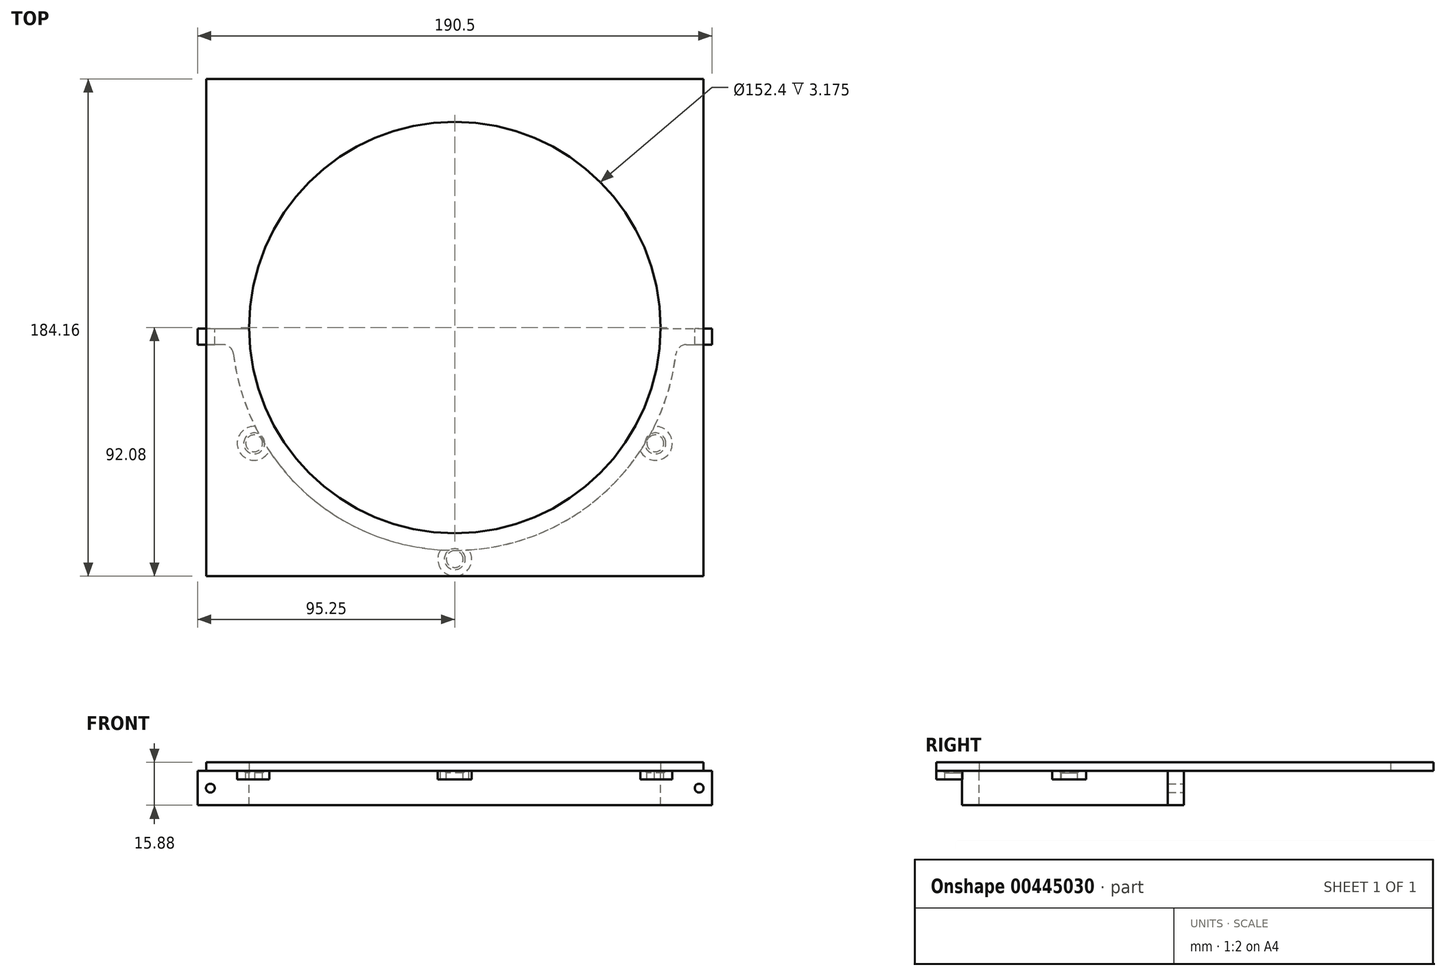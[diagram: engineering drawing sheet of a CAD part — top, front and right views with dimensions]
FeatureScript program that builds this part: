
annotation { "Feature Type Name" : "Feature", "Feature Type Description" : "" }
export const myFeature = defineFeature(function(context is Context, id is Id, definition is map)
    precondition{}
    {
        {
            var Q0;
            Q0=qCreatedBy(makeId("Top.planeOp"),FACE);
            var sketch = newSketch(context, id + "F0", { "sketchPlane" : qUnion([Q0])});
            skCircle(sketch, "E0", {"center": v(0, 0) * mm, "radius": 76.2 * mm});
            skCircle(sketch, "E1", {"center": v(0, 0) * mm, "radius": 82.55 * mm});
            skLineSegment(sketch, "E2.bottom", {"start": v(76.2, -6.35) * mm, "end": v(95.25, -6.35) * mm});
            skLineSegment(sketch, "E2.top", {"start": v(76.2, 6.35) * mm, "end": v(95.25, 6.35) * mm});
            skLineSegment(sketch, "E2.left", {"start": v(76.2, -6.35) * mm, "end": v(76.2, 6.35) * mm});
            skLineSegment(sketch, "E2.right", {"start": v(95.25, -6.35) * mm, "end": v(95.25, 6.35) * mm});
            skPoint(sketch, "E3", {"position": v(76.2, 0) * mm});
            skLineSegment(sketch, "E4.MirrorCS", {"start": v(-95.25, -6.35) * mm, "end": v(-95.25, 6.35) * mm});
            skLineSegment(sketch, "E5.MirrorCS", {"start": v(-76.2, -6.35) * mm, "end": v(-95.25, -6.35) * mm});
            skLineSegment(sketch, "E6.MirrorCS", {"start": v(-76.2, 6.35) * mm, "end": v(-95.25, 6.35) * mm});
            skCircle(sketch, "E7", {"center": v(-74.3, 42.9) * mm, "radius": 3.11 * mm});
            skLineSegment(sketch, "E8", {"start": v(-74.3, 42.9) * mm, "end": v(0, 0) * mm, "construction": true});
            skLineSegment(sketch, "E9", {"start": v(0, 0) * mm, "end": v(76.2, 0) * mm, "construction": true});
            skCircle(sketch, "E10.0", {"center": v(-74.3, 42.9) * mm, "radius": 6.29 * mm});
            skCircle(sketch, "E11.1.0", {"center": v(0, 85.79) * mm, "radius": 6.29 * mm});
            skCircle(sketch, "E11.1.1", {"center": v(0, 85.79) * mm, "radius": 3.11 * mm});
            skCircle(sketch, "E11.2.0", {"center": v(74.3, 42.9) * mm, "radius": 6.29 * mm});
            skCircle(sketch, "E11.2.1", {"center": v(74.3, 42.9) * mm, "radius": 3.11 * mm});
            skCircle(sketch, "E11.3.0", {"center": v(74.3, -42.9) * mm, "radius": 6.29 * mm});
            skCircle(sketch, "E11.3.1", {"center": v(74.3, -42.9) * mm, "radius": 3.11 * mm});
            skLineSegment(sketch, "E11.anchor2", {"start": v(-74.3, -42.9) * mm, "end": v(0, 0) * mm, "construction": true});
            skCircle(sketch, "E12.1.4.0", {"center": v(0, -85.79) * mm, "radius": 6.29 * mm});
            skCircle(sketch, "E12.2.4.0", {"center": v(0, -85.79) * mm, "radius": 3.11 * mm});
            skCircle(sketch, "E12.1.5.0", {"center": v(-74.3, -42.9) * mm, "radius": 6.29 * mm});
            skCircle(sketch, "E12.2.5.0", {"center": v(-74.3, -42.9) * mm, "radius": 3.11 * mm});
            skSolve(sketch);
        }
        {
            var Q0;
            Q0=makeQuery(id+"F0.imprint","IMPRINT",FACE,{"disambiguationData":[TD([[makeQuery(id+"F0.imprint","IMPRINT",EDGE,{"derivedFrom":sQuery(id+"F0.wireOp",EDGE,"E0")}),-1.0]])]});
            var Q1;
            {var subQ5=sQuery(id+"F0.wireOp",EDGE,"E2.right");Q1=makeQuery(id+"F0.imprint","IMPRINT",FACE,{"disambiguationData":[TD([[makeQuery(id+"F0.imprint","IMPRINT",EDGE,{"derivedFrom":subQ5}),1.0]])]});}
            var Q2;
            {var subQ3=sQuery(id+"F0.wireOp",EDGE,"E1");var subQ5=sQuery(id+"F0.wireOp",EDGE,"E2.bottom");var subQ7=makeQuery(id+"F0.imprint","INTERSECT",VERTEX,{"derivedFrom":[subQ3,subQ5]});Q2=makeQuery(id+"F0.imprint","IMPRINT",FACE,{"disambiguationData":[TD([[makeQuery(id+"F0.imprint","IMPRINT",EDGE,{"disambiguationData":[TD([[subQ7,-1.0]])],"derivedFrom":subQ3}),1.0]])]});}
            var Q3;
            {var subQ5=sQuery(id+"F0.wireOp",EDGE,"E4.MirrorCS");Q3=makeQuery(id+"F0.imprint","IMPRINT",FACE,{"disambiguationData":[TD([[makeQuery(id+"F0.imprint","IMPRINT",EDGE,{"derivedFrom":subQ5}),-1.0]])]});}
            var Q4;
            {var subQ0=sQuery(id+"F0.wireOp",EDGE,"E10.0");var subQ1=sQuery(id+"F0.wireOp",EDGE,"E1");var subQ2=makeQuery(id+"F0.imprint","INTERSECT",VERTEX,{"disambiguationData":[OD(0.0)],"derivedFrom":[subQ1,subQ0]});Q4=makeQuery(id+"F0.imprint","IMPRINT",FACE,{"disambiguationData":[TD([[makeQuery(id+"F0.imprint","IMPRINT",EDGE,{"disambiguationData":[TD([[subQ2,-1.0]])],"derivedFrom":subQ1}),1.0]])]});}
            var Q5;
            {var subQ0=sQuery(id+"F0.wireOp",EDGE,"E11.1.0");var subQ1=sQuery(id+"F0.wireOp",EDGE,"E1");var subQ2=makeQuery(id+"F0.imprint","INTERSECT",VERTEX,{"disambiguationData":[OD(0.0)],"derivedFrom":[subQ1,subQ0]});Q5=makeQuery(id+"F0.imprint","IMPRINT",FACE,{"disambiguationData":[TD([[makeQuery(id+"F0.imprint","IMPRINT",EDGE,{"disambiguationData":[TD([[subQ2,-1.0]])],"derivedFrom":subQ1}),1.0]])]});}
            var Q6;
            {var subQ0=sQuery(id+"F0.wireOp",EDGE,"E11.2.0");var subQ1=sQuery(id+"F0.wireOp",EDGE,"E1");var subQ2=makeQuery(id+"F0.imprint","INTERSECT",VERTEX,{"disambiguationData":[OD(0.0)],"derivedFrom":[subQ1,subQ0]});Q6=makeQuery(id+"F0.imprint","IMPRINT",FACE,{"disambiguationData":[TD([[makeQuery(id+"F0.imprint","IMPRINT",EDGE,{"disambiguationData":[TD([[subQ2,-1.0]])],"derivedFrom":subQ1}),1.0]])]});}
            var Q7;
            {var subQ0=sQuery(id+"F0.wireOp",EDGE,"E11.3.0");var subQ1=sQuery(id+"F0.wireOp",EDGE,"E1");var subQ2=makeQuery(id+"F0.imprint","INTERSECT",VERTEX,{"disambiguationData":[OD(0.0)],"derivedFrom":[subQ1,subQ0]});Q7=makeQuery(id+"F0.imprint","IMPRINT",FACE,{"disambiguationData":[TD([[makeQuery(id+"F0.imprint","IMPRINT",EDGE,{"disambiguationData":[TD([[subQ2,-1.0]])],"derivedFrom":subQ1}),1.0]])]});}
            var Q8;
            {var subQ0=sQuery(id+"F0.wireOp",EDGE,"E12.1.4.0");var subQ1=sQuery(id+"F0.wireOp",EDGE,"E1");var subQ2=makeQuery(id+"F0.imprint","INTERSECT",VERTEX,{"disambiguationData":[OD(0.0)],"derivedFrom":[subQ1,subQ0]});Q8=makeQuery(id+"F0.imprint","IMPRINT",FACE,{"disambiguationData":[TD([[makeQuery(id+"F0.imprint","IMPRINT",EDGE,{"disambiguationData":[TD([[subQ2,-1.0]])],"derivedFrom":subQ1}),1.0]])]});}
            var Q9;
            {var subQ0=sQuery(id+"F0.wireOp",EDGE,"E12.1.5.0");var subQ1=sQuery(id+"F0.wireOp",EDGE,"E1");var subQ2=makeQuery(id+"F0.imprint","INTERSECT",VERTEX,{"disambiguationData":[OD(0.0)],"derivedFrom":[subQ1,subQ0]});Q9=makeQuery(id+"F0.imprint","IMPRINT",FACE,{"disambiguationData":[TD([[makeQuery(id+"F0.imprint","IMPRINT",EDGE,{"disambiguationData":[TD([[subQ2,-1.0]])],"derivedFrom":subQ1}),1.0]])]});}
            extrude(context, id + "F1", {"entities" : qUnion([Q0, Q1, Q2, Q3, Q4, Q5, Q6, Q7, Q8, Q9]), "oppositeDirection" : true, "depth" : 12.7 * mm, "offsetDistance" : 25.4 * mm});
        }
        {
            var Q0;
            Q0=makeQuery(id+"F0.imprint","IMPRINT",FACE,{"disambiguationData":[TD([[makeQuery(id+"F0.imprint","IMPRINT",EDGE,{"derivedFrom":sQuery(id+"F0.wireOp",EDGE,"E7")}),-1.0]])]});
            var Q1;
            Q1=makeQuery(id+"F0.imprint","IMPRINT",FACE,{"disambiguationData":[TD([[makeQuery(id+"F0.imprint","IMPRINT",EDGE,{"derivedFrom":sQuery(id+"F0.wireOp",EDGE,"E11.1.1")}),-1.0]])]});
            var Q2;
            Q2=makeQuery(id+"F0.imprint","IMPRINT",FACE,{"disambiguationData":[TD([[makeQuery(id+"F0.imprint","IMPRINT",EDGE,{"derivedFrom":sQuery(id+"F0.wireOp",EDGE,"E11.2.1")}),-1.0]])]});
            var Q3;
            Q3=makeQuery(id+"F0.imprint","IMPRINT",FACE,{"disambiguationData":[TD([[makeQuery(id+"F0.imprint","IMPRINT",EDGE,{"derivedFrom":sQuery(id+"F0.wireOp",EDGE,"E11.3.1")}),-1.0]])]});
            var Q4;
            Q4=makeQuery(id+"F0.imprint","IMPRINT",FACE,{"disambiguationData":[TD([[makeQuery(id+"F0.imprint","IMPRINT",EDGE,{"derivedFrom":sQuery(id+"F0.wireOp",EDGE,"E12.2.4.0")}),-1.0]])]});
            var Q5;
            Q5=makeQuery(id+"F0.imprint","IMPRINT",FACE,{"disambiguationData":[TD([[makeQuery(id+"F0.imprint","IMPRINT",EDGE,{"derivedFrom":sQuery(id+"F0.wireOp",EDGE,"E12.2.5.0")}),-1.0]])]});
            extrude(context, id + "F2", {"entities" : qUnion([Q0, Q1, Q2, Q3, Q4, Q5]), "operationType" : NewBodyOperationType.ADD, "oppositeDirection" : true, "depth" : 3.17 * mm, "offsetDistance" : 25.4 * mm});
        }
        {
            var Q0;
            {var subQ0=sQuery(id+"F0.wireOp",EDGE,"E12.1.4.0");var subQ1=sQuery(id+"F0.wireOp",EDGE,"E1");Q0=makeQuery(id+"F2.opExtrude","SWEPT_EDGE",EDGE,{"disambiguationData":[OSD([subQ1,subQ0]),TDD([makeQuery(id+"F0.imprint","INTERSECT",VERTEX,{"disambiguationData":[OD(0.0)],"derivedFrom":[subQ1,subQ0]})])]});}
            var Q1;
            {var subQ0=sQuery(id+"F0.wireOp",EDGE,"E12.1.4.0");var subQ1=sQuery(id+"F0.wireOp",EDGE,"E1");Q1=makeQuery(id+"F2.opExtrude","CAP_EDGE",EDGE,{"disambiguationData":[OSD([subQ1]),TDD([makeQuery(id+"F0.imprint","IMPRINT",EDGE,{"disambiguationData":[TD([[makeQuery(id+"F0.imprint","INTERSECT",VERTEX,{"disambiguationData":[OD(0.0)],"derivedFrom":[subQ1,subQ0]}),-1.0]])],"derivedFrom":subQ1})])],"isStart":false});}
            var Q2;
            {var subQ0=sQuery(id+"F0.wireOp",EDGE,"E12.1.4.0");var subQ1=sQuery(id+"F0.wireOp",EDGE,"E1");Q2=makeQuery(id+"F2.opExtrude","SWEPT_EDGE",EDGE,{"disambiguationData":[OSD([subQ1,subQ0]),TDD([makeQuery(id+"F0.imprint","INTERSECT",VERTEX,{"disambiguationData":[OD(1.0)],"derivedFrom":[subQ1,subQ0]})])]});}
            var Q3;
            {var subQ0=sQuery(id+"F0.wireOp",EDGE,"E12.1.5.0");var subQ1=sQuery(id+"F0.wireOp",EDGE,"E1");Q3=makeQuery(id+"F2.opExtrude","SWEPT_EDGE",EDGE,{"disambiguationData":[OSD([subQ1,subQ0]),TDD([makeQuery(id+"F0.imprint","INTERSECT",VERTEX,{"disambiguationData":[OD(1.0)],"derivedFrom":[subQ1,subQ0]})])]});}
            var Q4;
            {var subQ0=sQuery(id+"F0.wireOp",EDGE,"E12.1.5.0");var subQ1=sQuery(id+"F0.wireOp",EDGE,"E1");Q4=makeQuery(id+"F2.opExtrude","CAP_EDGE",EDGE,{"disambiguationData":[OSD([subQ1]),TDD([makeQuery(id+"F0.imprint","IMPRINT",EDGE,{"disambiguationData":[TD([[makeQuery(id+"F0.imprint","INTERSECT",VERTEX,{"disambiguationData":[OD(0.0)],"derivedFrom":[subQ1,subQ0]}),-1.0]])],"derivedFrom":subQ1})])],"isStart":false});}
            var Q5;
            {var subQ0=sQuery(id+"F0.wireOp",EDGE,"E12.1.5.0");var subQ1=sQuery(id+"F0.wireOp",EDGE,"E1");Q5=makeQuery(id+"F2.opExtrude","SWEPT_EDGE",EDGE,{"disambiguationData":[OSD([subQ1,subQ0]),TDD([makeQuery(id+"F0.imprint","INTERSECT",VERTEX,{"disambiguationData":[OD(0.0)],"derivedFrom":[subQ1,subQ0]})])]});}
            var Q6;
            Q6=makeQuery(id+"F1.opExtrude","SWEPT_EDGE",EDGE,{"disambiguationData":[OSD([sQuery(id+"F0.wireOp",EDGE,"E1"),sQuery(id+"F0.wireOp",EDGE,"E5.MirrorCS")])]});
            var Q7;
            {var subQ0=sQuery(id+"F0.wireOp",EDGE,"E11.3.0");var subQ1=sQuery(id+"F0.wireOp",EDGE,"E1");Q7=makeQuery(id+"F2.opExtrude","SWEPT_EDGE",EDGE,{"disambiguationData":[OSD([subQ1,subQ0]),TDD([makeQuery(id+"F0.imprint","INTERSECT",VERTEX,{"disambiguationData":[OD(1.0)],"derivedFrom":[subQ1,subQ0]})])]});}
            var Q8;
            {var subQ0=sQuery(id+"F0.wireOp",EDGE,"E11.3.0");var subQ1=sQuery(id+"F0.wireOp",EDGE,"E1");Q8=makeQuery(id+"F2.opExtrude","SWEPT_EDGE",EDGE,{"disambiguationData":[OSD([subQ1,subQ0]),TDD([makeQuery(id+"F0.imprint","INTERSECT",VERTEX,{"disambiguationData":[OD(0.0)],"derivedFrom":[subQ1,subQ0]})])]});}
            var Q9;
            {var subQ0=sQuery(id+"F0.wireOp",EDGE,"E11.3.0");var subQ1=sQuery(id+"F0.wireOp",EDGE,"E1");Q9=makeQuery(id+"F2.opExtrude","CAP_EDGE",EDGE,{"disambiguationData":[OSD([subQ1]),TDD([makeQuery(id+"F0.imprint","IMPRINT",EDGE,{"disambiguationData":[TD([[makeQuery(id+"F0.imprint","INTERSECT",VERTEX,{"disambiguationData":[OD(0.0)],"derivedFrom":[subQ1,subQ0]}),-1.0]])],"derivedFrom":subQ1})])],"isStart":false});}
            var Q10;
            Q10=makeQuery(id+"F1.opExtrude","SWEPT_EDGE",EDGE,{"disambiguationData":[OSD([sQuery(id+"F0.wireOp",EDGE,"E1"),sQuery(id+"F0.wireOp",EDGE,"E2.bottom")])]});
            fillet(context, id + "F3", {"entities" : qUnion([Q0, Q1, Q2, Q3, Q4, Q5, Q6, Q7, Q8, Q9, Q10]), "radius" : 3.8 * mm, "tangentPropagation" : true, "allowEdgeOverflow" : false});
        }
        {
            var Q0;
            Q0=makeQuery(id+"F1.opExtrude","SWEPT_FACE",FACE,{"disambiguationData":[OSD([sQuery(id+"F0.wireOp",EDGE,"E2.bottom")])]});
            var sketch = newSketch(context, id + "F4", { "sketchPlane" : qUnion([Q0])});
            skPoint(sketch, "E13", {"position": v(90.5, -6.35) * mm});
            skPoint(sketch, "E13.positionSnap0", {"position": v(95.25, -6.35) * mm});
            skPoint(sketch, "E13.positionSnap1", {"position": v(90.5, -12.7) * mm});
            skPoint(sketch, "E14.MirrorP", {"position": v(-90.5, -6.35) * mm});
            skSolve(sketch);
        }
        {
            var Q0;
            Q0=sQuery(id+"F4.wireOp",VERTEX,"E14.MirrorP");
            var Q1;
            Q1=sQuery(id+"F4.wireOp",VERTEX,"E13");
            var Q2;
            Q2=makeQuery(id+"F1.opExtrude","SWEPT_BODY",BODY,{"disambiguationData":[OSD([sQuery(id+"F0.wireOp",EDGE,"E0"),sQuery(id+"F0.wireOp",EDGE,"E1"),sQuery(id+"F0.wireOp",EDGE,"E2.bottom"),sQuery(id+"F0.wireOp",EDGE,"E2.top"),sQuery(id+"F0.wireOp",EDGE,"E2.right"),sQuery(id+"F0.wireOp",EDGE,"E4.MirrorCS"),sQuery(id+"F0.wireOp",EDGE,"E5.MirrorCS"),sQuery(id+"F0.wireOp",EDGE,"E6.MirrorCS")])]});
            hole(context, id + "F5", {"style" : HoleStyle.SIMPLE, "endStyle" : HoleEndStyle.THROUGH, "standardTappedOrClearance" : lookupTablePath({ "standard" : "ANSI", "fit" : "Normal (ASME)", "size" : "#4", "type" : "Clearance" }), "standardBlindInLast" : lookupTablePath({ "fit" : "Free", "standard" : "ANSI", "size" : "#4", "type" : "Clearance" }), "holeDiameter" : 3.26 * mm, "isTappedThrough" : true, "tappedDepth" : 12.7 * mm, "tapClearance" : 3, "locations" : qUnion([Q0, Q1]), "scope" : qUnion([Q2]), "startStyle" : HoleStartStyle.PART});
        }
        {
            var Q0;
            Q0=makeQuery(id+"F2.opExtrude","CAP_EDGE",EDGE,{"disambiguationData":[OSD([sQuery(id+"F0.wireOp",EDGE,"E12.2.4.0")])],"isStart":true});
            var Q1;
            Q1=makeQuery(id+"F2.opExtrude","CAP_EDGE",EDGE,{"disambiguationData":[OSD([sQuery(id+"F0.wireOp",EDGE,"E12.2.5.0")])],"isStart":true});
            var Q2;
            Q2=makeQuery(id+"F2.opExtrude","CAP_EDGE",EDGE,{"disambiguationData":[OSD([sQuery(id+"F0.wireOp",EDGE,"E11.3.1")])],"isStart":true});
            chamfer(context, id + "F6", {"entities" : qUnion([Q0, Q1, Q2]), "width" : 0.76 * mm, "tangentPropagation" : true});
        }
        {
            var Q0;
            Q0=qCreatedBy(makeId("Front.planeOp"),FACE);
            var sketch = newSketch(context, id + "F7", { "sketchPlane" : qUnion([Q0])});
            skPoint(sketch, "E15.0", {"position": v(-95.25, 0) * mm});
            skPoint(sketch, "E16.0", {"position": v(95.25, -12.7) * mm});
            skLineSegment(sketch, "E17.bottom", {"start": v(-95.25, 0) * mm, "end": v(95.25, 0) * mm});
            skLineSegment(sketch, "E17.top", {"start": v(-95.25, -12.7) * mm, "end": v(95.25, -12.7) * mm});
            skLineSegment(sketch, "E17.left", {"start": v(-95.25, 0) * mm, "end": v(-95.25, -12.7) * mm});
            skLineSegment(sketch, "E17.right", {"start": v(95.25, 0) * mm, "end": v(95.25, -12.7) * mm});
            skSolve(sketch);
        }
        {
            var Q0;
            Q0=makeQuery(id+"F7.imprint","IMPRINT",FACE,{"disambiguationData":[TD([[makeQuery(id+"F7.imprint","IMPRINT",EDGE,{"derivedFrom":sQuery(id+"F7.wireOp",EDGE,"E17.bottom")}),-1.0]])]});
            extrude(context, id + "F8", {"entities" : qUnion([Q0]), "operationType" : NewBodyOperationType.REMOVE, "endBound" : BoundingType.THROUGH_ALL, "oppositeDirection" : true, "depth" : 25.4 * mm, "offsetDistance" : 25.4 * mm, "hasSecondDirection" : true, "secondDirectionOppositeDirection" : false, "secondDirectionDepth" : 0.38 * mm});
        }
        {
            var Q0;
            Q0=qCreatedBy(makeId("Top.planeOp"),FACE);
            var sketch = newSketch(context, id + "F9", { "sketchPlane" : qUnion([Q0])});
            skLineSegment(sketch, "E18.bottom", {"start": v(92.07, -92.07) * mm, "end": v(-92.08, -92.08) * mm});
            skLineSegment(sketch, "E18.top", {"start": v(92.08, 92.08) * mm, "end": v(-92.07, 92.08) * mm});
            skLineSegment(sketch, "E18.left", {"start": v(92.08, -92.07) * mm, "end": v(92.08, 92.08) * mm});
            skLineSegment(sketch, "E18.right", {"start": v(-92.08, -92.08) * mm, "end": v(-92.08, 92.07) * mm});
            skPoint(sketch, "E18.middle", {"position": v(0, 0) * mm});
            skCircle(sketch, "E19", {"center": v(0, 0) * mm, "radius": 76.2 * mm});
            skSolve(sketch);
        }
        {
            var Q0;
            Q0=makeQuery(id+"F9.imprint","IMPRINT",FACE,{"disambiguationData":[TD([[makeQuery(id+"F9.imprint","IMPRINT",EDGE,{"derivedFrom":sQuery(id+"F9.wireOp",EDGE,"E18.bottom")}),-1.0]])]});
            extrude(context, id + "F10", {"entities" : qUnion([Q0]), "depth" : 3.17 * mm});
        }
    });
